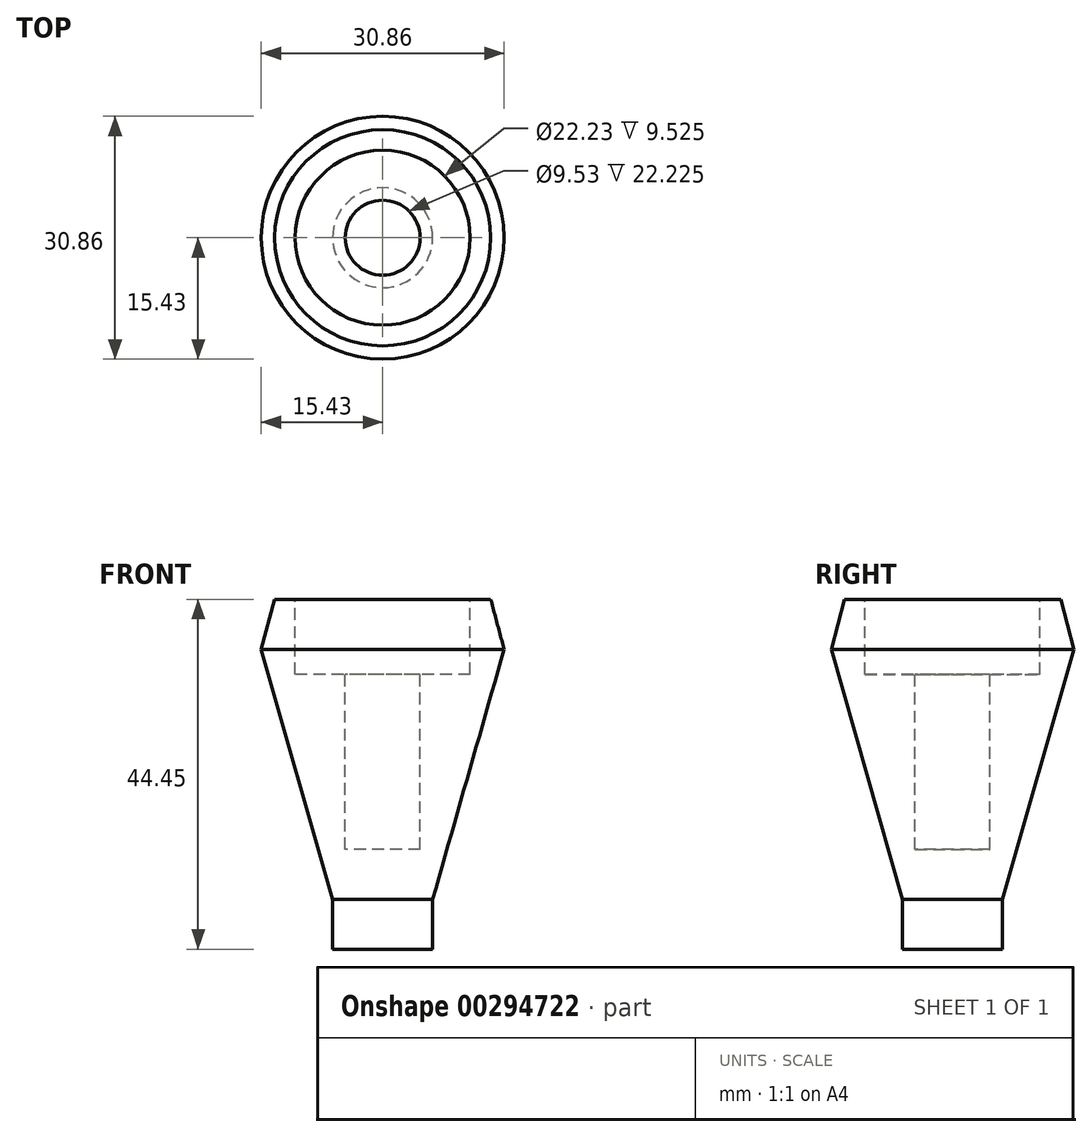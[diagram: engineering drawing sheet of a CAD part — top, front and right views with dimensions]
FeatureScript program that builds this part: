
annotation { "Feature Type Name" : "Feature", "Feature Type Description" : "" }
export const myFeature = defineFeature(function(context is Context, id is Id, definition is map)
    precondition{}
    {
        {
            var Q0;
            Q0=qCreatedBy(makeId("Front.planeOp"),FACE);
            var sketch = newSketch(context, id + "F0", { "sketchPlane" : qUnion([Q0])});
            skLineSegment(sketch, "E0", {"start": v(-6.35, -15.02) * mm, "end": v(0, -15.02) * mm});
            skLineSegment(sketch, "E1", {"start": v(0, -15.02) * mm, "end": v(0, -8.67) * mm});
            skLineSegment(sketch, "E2", {"start": v(0, -8.67) * mm, "end": v(9.08, 23.08) * mm});
            skLineSegment(sketch, "E3", {"start": v(9.08, 23.08) * mm, "end": v(7.38, 29.43) * mm});
            skLineSegment(sketch, "E4", {"start": v(7.38, 29.43) * mm, "end": v(7.38, 29.43) * mm});
            skLineSegment(sketch, "E5", {"start": v(7.38, 29.43) * mm, "end": v(-6.35, 29.43) * mm});
            skLineSegment(sketch, "E6", {"start": v(-6.35, 29.43) * mm, "end": v(-6.35, -15.02) * mm});
            skSolve(sketch);
        }
        {
            var Q0;
            Q0=makeQuery(id+"F0.imprint","IMPRINT",FACE,{"disambiguationData":[TD([[makeQuery(id+"F0.imprint","IMPRINT",EDGE,{"derivedFrom":sQuery(id+"F0.wireOp",EDGE,"E0")}),1.0]])]});
            var Q1;
            Q1=sQuery(id+"F0.wireOp",EDGE,"E6");
            revolve(context, id + "F1", {"entities" : qUnion([Q0]), "axis" : qUnion([Q1]), "revolveType" : RevolveType.FULL});
        }
        {
            var Q0;
            Q0=makeQuery(id+"F1.opRevolve","SWEPT_FACE",FACE,{"disambiguationData":[OSD([sQuery(id+"F0.wireOp",EDGE,"E5")])]});
            var sketch = newSketch(context, id + "F2", { "sketchPlane" : qUnion([Q0])});
            skCircle(sketch, "E7", {"center": v(-6.35, 0) * mm, "radius": 11.11 * mm});
            skCircle(sketch, "E8", {"center": v(-6.35, 0) * mm, "radius": 4.76 * mm});
            skSolve(sketch);
        }
        {
            var Q0;
            Q0=makeQuery(id+"F2.imprint","IMPRINT",FACE,{"disambiguationData":[TD([[makeQuery(id+"F2.imprint","IMPRINT",EDGE,{"derivedFrom":sQuery(id+"F2.wireOp",EDGE,"E7")}),1.0]])]});
            extrude(context, id + "F3", {"entities" : qUnion([Q0]), "operationType" : NewBodyOperationType.REMOVE, "oppositeDirection" : true, "depth" : 9.52 * mm});
        }
        {
            var Q0;
            Q0=makeQuery(id+"F3.boolean.opBoolean","SPLIT",FACE,{"disambiguationData":[TD([makeQuery(id+"F3.opExtrude","SWEPT_FACE",FACE,{"disambiguationData":[OSD([sQuery(id+"F2.wireOp",EDGE,"E8")])]})])],"derivedFrom":makeQuery(id+"F1.opRevolve","SWEPT_FACE",FACE,{"disambiguationData":[OSD([sQuery(id+"F0.wireOp",EDGE,"E5")])]})});
            extrude(context, id + "F4", {"entities" : qUnion([Q0]), "operationType" : NewBodyOperationType.REMOVE, "oppositeDirection" : true, "depth" : 31.75 * mm});
        }
    });
